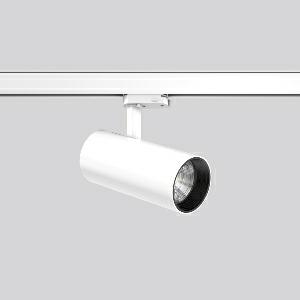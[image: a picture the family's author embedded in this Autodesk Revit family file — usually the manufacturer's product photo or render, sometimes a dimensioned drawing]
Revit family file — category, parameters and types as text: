
# Revit family: deecos_s_mini_742207_002_2_76_d836
name_source: partatom
category: Lighting Fixtures
units: mm (PartAtom-declared; Revit-internal decimal feet)

## family parameters
Cut with Voids When Loaded = No
Host = Face
Light Source = No
Part Type = Normal
Room Calculation Point = No
Round Connector Dimension = Use Diameter
Shared = No

## types (1)
- DEECOS S mini (1 x LED Modul 927, 2850 lm, 2700)
    Apparent Load = 29 VA
    Approval mark = CE
    CIE Flux Codes = 96 100 100 100 100
    Color Rendering = 92
    Color Temperature = 2700
    Default Elevation = 1800 mm
    Description = Series: DEECOS S mini
LED surface-mounted projector in modern design with no visible cooling ribs. Housing: die-cast aluminium, powder-coated. Rotation range: 356°. Swivel range: 90°. Black plastic ring and recessed LED to prevent glare from the side. Optical assembly with lens made of plastic (polycarbonate) for the best homogeneous light distribution - can be changed without tools. Best colour rendering index Ra>90. With adapter for RZB 3-circuit DALI tracks. Suitable for Track on ceiling, Wall track. High quality converter without flickering and stroboscopic effect. The following accessories can be mounted without use of tools: interchangeable lenses, decorative glasses, honeycomb louvre, clear and frosted diffusers, white interchangeable plastic ring. 
Colour: traffic white, matt (RAL 9016)
Diameter: 87 mm
Height: 214 mm
Lamp: LED
Socket: without socket
Colour temperature: 2700K
Colour rendering index (CRI): 92
System power: 29 W
Rated luminous flux: 2850 lm
Luminous efficiency: 98 lm/W
Control gear: Converter, dimmable, DALI
Protection class: I
Type of protection: IP 20
    Height = 214 mm
    Lamp = 1 x LED Modul 927
    Lamp Light Flux = 2850 lm
    Lamp count = 1
    Length = 87 mm
    Lifetime = 50000 h
    Luminous efficacy = 98 lm/W
    Manufacturer = RZB
    ModVariant = No
    Model = 742207.002.2.76
    Mounting Place = Ceiling
    Mounting Type = Rail mounted
    Number of Poles = 1
    OnlyDefault = Yes
    Power Factor = 1
    Product Name = DEECOS S mini
    Product group = Track mounted projectors
    ProductGroupID = 301
    Protection Class = Protection class I
    Protection Degree = IP 20
    RLX_Detail_Level = 1
    RLX_Emergency_Light_Flux = 0 lm
    RLX_Emergency_Type = 0
    RLX_Emergency_Type_DB = No
    RlxData = <blob elided: 35481 chars, md5=71c238b0>
    Socket = socket
    Standby Power = 0 W
    System Light Flux = 2850 lm
    System Power = 29 W
    Type Comments = Product without accessories
    Type Image = 741930.002.jpg
    URL = http://relux.com
    VarID = ---
    Voltage = 230 V
    Voltage Range = 220-240 V
    Weight = 0.00 kg
    Width = 0 mm  [stored 0 ft]

note: [stored X ft] marks values corroborated as IEEE doubles in the binary element streams (Revit-internal decimal feet)

## geometry (parser evidence)
native form markers: Blend x4, Sweep x13
no freeform markers — native parametric forms only
